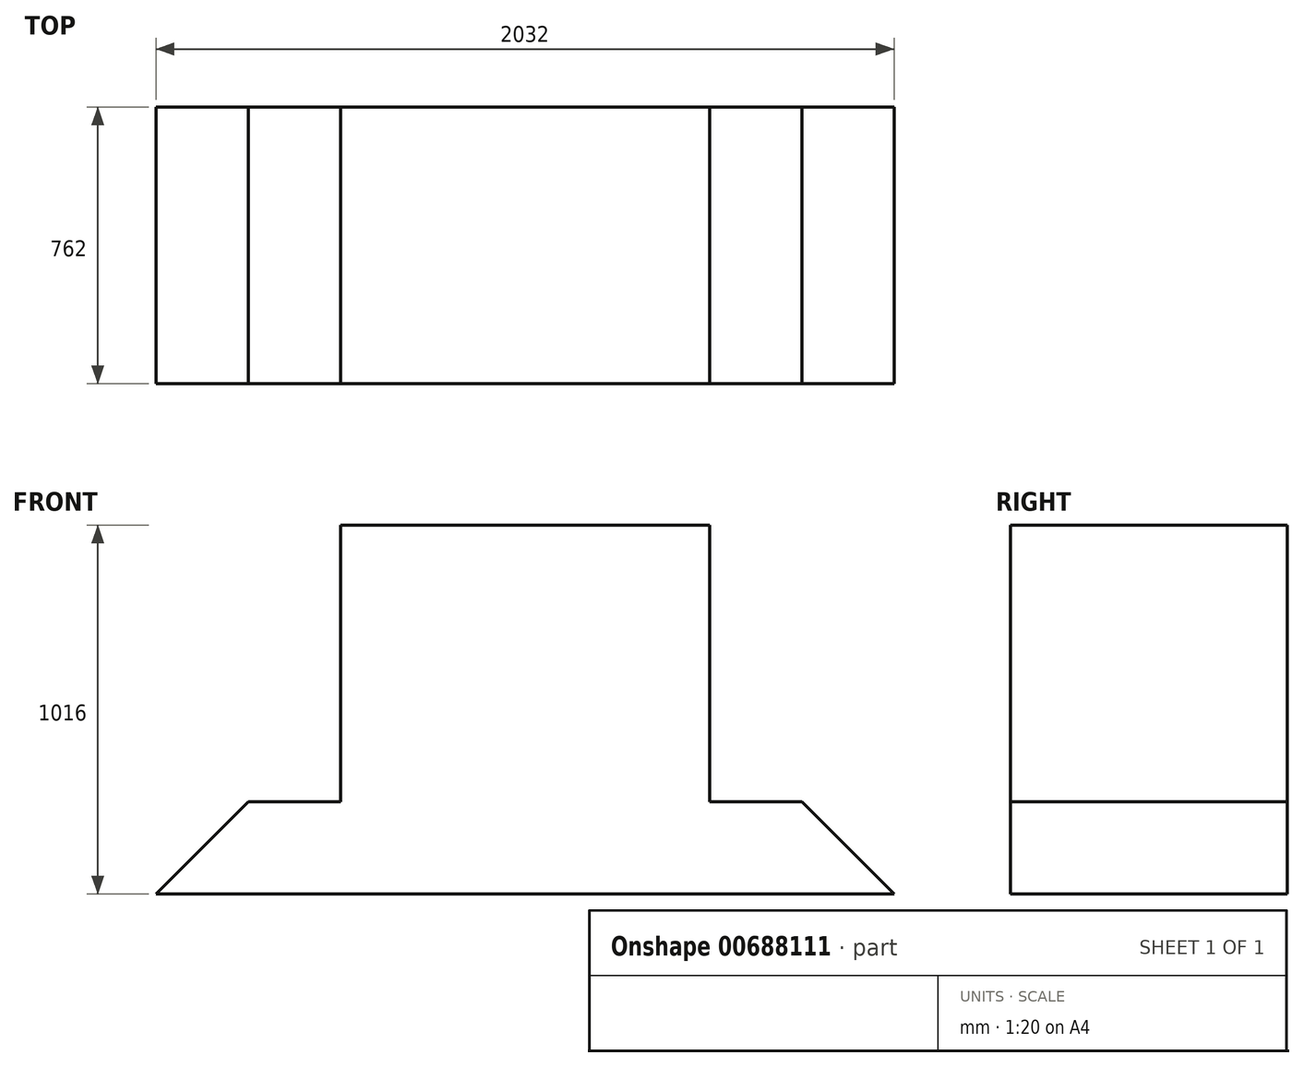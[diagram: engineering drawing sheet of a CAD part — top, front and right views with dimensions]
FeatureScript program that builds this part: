
annotation { "Feature Type Name" : "Feature", "Feature Type Description" : "" }
export const myFeature = defineFeature(function(context is Context, id is Id, definition is map)
    precondition{}
    {
        {
            var Q0;
            Q0=qCreatedBy(makeId("Front.planeOp"),FACE);
            var sketch = newSketch(context, id + "F0", { "sketchPlane" : qUnion([Q0])});
            skLineSegment(sketch, "E0", {"start": v(0, 0) * mm, "end": v(2032, 0) * mm});
            skLineSegment(sketch, "E1", {"start": v(2032, 0) * mm, "end": v(1778, 254) * mm});
            skLineSegment(sketch, "E2", {"start": v(1778, 254) * mm, "end": v(1524, 254) * mm});
            skLineSegment(sketch, "E3", {"start": v(1524, 254) * mm, "end": v(1524, 1016) * mm});
            skLineSegment(sketch, "E4", {"start": v(1524, 1016) * mm, "end": v(508, 1016) * mm});
            skLineSegment(sketch, "E5", {"start": v(508, 1016) * mm, "end": v(508, 254) * mm});
            skLineSegment(sketch, "E6", {"start": v(508, 254) * mm, "end": v(254, 254) * mm});
            skLineSegment(sketch, "E7", {"start": v(254, 254) * mm, "end": v(0, 0) * mm});
            skSolve(sketch);
        }
        {
            var Q0;
            Q0 = qSketchRegion(id + "F0", true);
            extrude(context, id + "F1", {"entities" : qUnion([Q0]), "depth" : 762 * mm, "offsetDistance" : 25.4 * mm});
        }
    });
